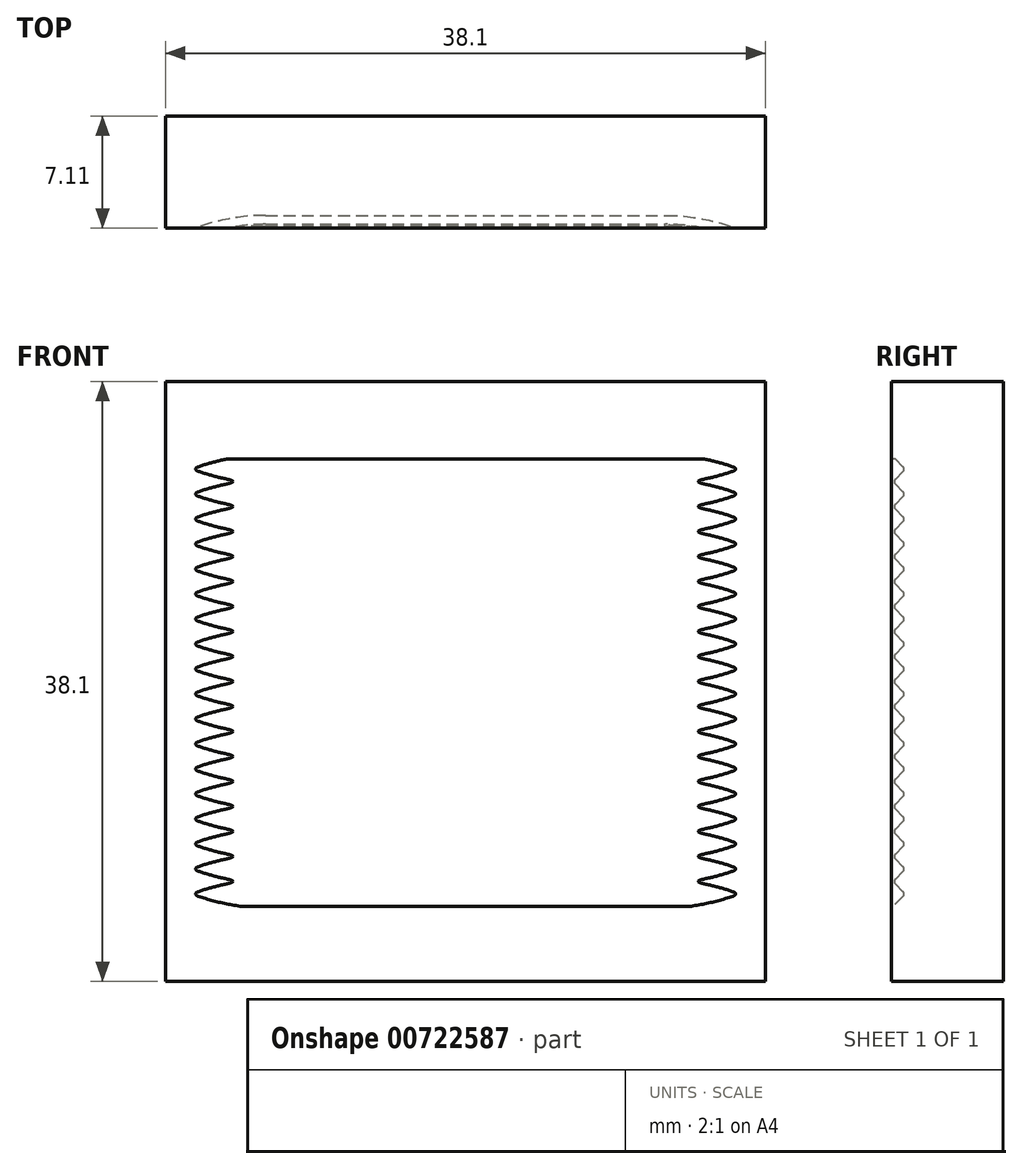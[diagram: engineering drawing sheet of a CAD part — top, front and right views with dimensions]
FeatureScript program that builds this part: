
annotation { "Feature Type Name" : "Feature", "Feature Type Description" : "" }
export const myFeature = defineFeature(function(context is Context, id is Id, definition is map)
    precondition{}
    {
        {
            var Q0;
            Q0=qCreatedBy(makeId("Front.planeOp"),FACE);
            var sketch = newSketch(context, id + "F0", { "sketchPlane" : qUnion([Q0])});
            skLineSegment(sketch, "E0", {"start": v(-12.7, -25.4) * mm, "end": v(-12.7, -12.7) * mm});
            skLineSegment(sketch, "E1", {"start": v(-12.7, 25.4) * mm, "end": v(12.7, 25.4) * mm});
            skLineSegment(sketch, "E2", {"start": v(12.7, 25.4) * mm, "end": v(12.7, 12.7) * mm});
            skLineSegment(sketch, "E3", {"start": v(12.7, -25.4) * mm, "end": v(-12.7, -25.4) * mm});
            skLineSegment(sketch, "E4", {"start": v(0, -25.4) * mm, "end": v(0, 25.4) * mm, "construction": true});
            skLineSegment(sketch, "E5", {"start": v(-12.7, 12.7) * mm, "end": v(12.7, 12.7) * mm, "construction": true});
            skLineSegment(sketch, "E6", {"start": v(-12.7, -12.7) * mm, "end": v(12.7, -12.7) * mm, "construction": true});
            skLineSegment(sketch, "E7", {"start": v(-25.4, 0) * mm, "end": v(25.4, 0) * mm, "construction": true});
            skPoint(sketch, "E8.orphan", {"position": v(0, 47.84) * mm});
            skLineSegment(sketch, "E9", {"start": v(-25.4, -12.7) * mm, "end": v(-25.4, 12.7) * mm});
            skLineSegment(sketch, "E10", {"start": v(-25.4, 12.7) * mm, "end": v(-12.7, 12.7) * mm});
            skLineSegment(sketch, "E11", {"start": v(25.4, 12.7) * mm, "end": v(25.4, -12.7) * mm});
            skLineSegment(sketch, "E12", {"start": v(25.4, -12.7) * mm, "end": v(12.7, -12.7) * mm});
            skLineSegment(sketch, "E13.trimOffspring", {"start": v(12.7, 12.7) * mm, "end": v(25.4, 12.7) * mm});
            skLineSegment(sketch, "E14.trimOffspring", {"start": v(12.7, -12.7) * mm, "end": v(12.7, -25.4) * mm});
            skLineSegment(sketch, "E15.trimOffspring", {"start": v(-12.7, 12.7) * mm, "end": v(-12.7, 25.4) * mm});
            skLineSegment(sketch, "E16.trimOffspring", {"start": v(-12.7, -12.7) * mm, "end": v(-25.4, -12.7) * mm});
            skLineSegment(sketch, "E17", {"start": v(-12.7, 12.7) * mm, "end": v(-12.7, -12.7) * mm, "construction": true});
            skLineSegment(sketch, "E18", {"start": v(12.7, 12.7) * mm, "end": v(12.7, -12.7) * mm, "construction": true});
            skCircle(sketch, "E19", {"center": v(0, 0) * mm, "radius": 12.7 * mm, "construction": true});
            skSolve(sketch);
        }
        {
            var Q0;
            Q0 = qSketchRegion(id + "F0", true);
            extrude(context, id + "F1", {"entities" : qUnion([Q0]), "depth" : 12.7 * mm, "offsetDistance" : 25.4 * mm});
        }
        {
            var Q0;
            Q0=qCreatedBy(makeId("Front.planeOp"),FACE);
            var sketch = newSketch(context, id + "F2", { "sketchPlane" : qUnion([Q0])});
            skLineSegment(sketch, "E20.bottom", {"start": v(-12.7, 12.7) * mm, "end": v(12.7, 12.7) * mm, "construction": true});
            skLineSegment(sketch, "E20.top", {"start": v(-12.7, -12.7) * mm, "end": v(12.7, -12.7) * mm, "construction": true});
            skLineSegment(sketch, "E20.left", {"start": v(-12.7, 12.7) * mm, "end": v(-12.7, -12.7) * mm, "construction": true});
            skLineSegment(sketch, "E20.right", {"start": v(12.7, 12.7) * mm, "end": v(12.7, -12.7) * mm, "construction": true});
            skLineSegment(sketch, "E21.bottom", {"start": v(19.05, 19.05) * mm, "end": v(-19.05, 19.05) * mm});
            skLineSegment(sketch, "E21.top", {"start": v(19.05, -19.05) * mm, "end": v(-19.05, -19.05) * mm});
            skLineSegment(sketch, "E21.left", {"start": v(19.05, 19.05) * mm, "end": v(19.05, -19.05) * mm});
            skLineSegment(sketch, "E21.right", {"start": v(-19.05, 19.05) * mm, "end": v(-19.05, -19.05) * mm});
            skLineSegment(sketch, "E22", {"start": v(-19.05, 19.05) * mm, "end": v(19.05, -19.05) * mm, "construction": true});
            skLineSegment(sketch, "E23", {"start": v(-19.05, -19.05) * mm, "end": v(19.05, 19.05) * mm, "construction": true});
            skSolve(sketch);
        }
        {
            var Q0;
            Q0=makeQuery(id+"F1.opExtrude","CAP_EDGE",EDGE,{"disambiguationData":[OSD([sQuery(id+"F0.wireOp",EDGE,"E9")])],"isStart":true});
            var Q1;
            Q1=makeQuery(id+"F1.opExtrude","CAP_EDGE",EDGE,{"disambiguationData":[OSD([sQuery(id+"F0.wireOp",EDGE,"E3")])],"isStart":true});
            var Q2;
            Q2=makeQuery(id+"F1.opExtrude","CAP_EDGE",EDGE,{"disambiguationData":[OSD([sQuery(id+"F0.wireOp",EDGE,"E1")])],"isStart":true});
            var Q3;
            Q3=makeQuery(id+"F1.opExtrude","CAP_EDGE",EDGE,{"disambiguationData":[OSD([sQuery(id+"F0.wireOp",EDGE,"E11")])],"isStart":true});
            fillet(context, id + "F3", {"entities" : qUnion([Q0, Q1, Q2, Q3]), "radius" : 12.7 * mm, "tangentPropagation" : true, "allowEdgeOverflow" : false});
        }
        {
            var Q0;
            Q0 = qSketchRegion(id + "F2", true);
            extrude(context, id + "F4", {"entities" : qUnion([Q0]), "oppositeDirection" : true, "depth" : 6.35 * mm, "offsetDistance" : 25.4 * mm, "hasSecondDirection" : true, "secondDirectionOppositeDirection" : false, "secondDirectionDepth" : 0.76 * mm});
        }
        {
            var Q0;
            Q0=makeQuery(id+"F1.opExtrude","CAP_FACE",FACE,{"disambiguationData":[OSD([sQuery(id+"F0.wireOp",EDGE,"E0"),sQuery(id+"F0.wireOp",EDGE,"E1"),sQuery(id+"F0.wireOp",EDGE,"E2"),sQuery(id+"F0.wireOp",EDGE,"E3"),sQuery(id+"F0.wireOp",EDGE,"E9"),sQuery(id+"F0.wireOp",EDGE,"E10"),sQuery(id+"F0.wireOp",EDGE,"E11"),sQuery(id+"F0.wireOp",EDGE,"E12"),sQuery(id+"F0.wireOp",EDGE,"E13.trimOffspring"),sQuery(id+"F0.wireOp",EDGE,"E14.trimOffspring"),sQuery(id+"F0.wireOp",EDGE,"E15.trimOffspring"),sQuery(id+"F0.wireOp",EDGE,"E16.trimOffspring")])],"isStart":false});
            var sketch = newSketch(context, id + "F5", { "sketchPlane" : qUnion([Q0])});
            skLineSegment(sketch, "E24", {"start": v(-24.88, -12.56) * mm, "end": v(-25.38, -12.05) * mm});
            skLineSegment(sketch, "E25", {"start": v(-24.88, -12.84) * mm, "end": v(-25.38, -13.35) * mm});
            skLineSegment(sketch, "E26", {"start": v(-19.18, -13.5) * mm, "end": v(-25.53, -13.5) * mm, "construction": true});
            skPoint(sketch, "E27.visualSharp", {"position": v(-24.73, -12.7) * mm});
            skArc(sketch, "E27.filletArc", {"start": v(-24.88, -12.84) * mm, "mid": v(-24.82, -12.7) * mm, "end": v(-24.88, -12.56) * mm});
            skLineSegment(sketch, "E28", {"start": v(-19.18, -14.29) * mm, "end": v(-19.18, 14.14) * mm});
            skLineSegment(sketch, "E29", {"start": v(-25.38, -13.64) * mm, "end": v(-24.73, -14.29) * mm});
            skLineSegment(sketch, "E30", {"start": v(-24.73, -14.29) * mm, "end": v(-19.18, -14.29) * mm});
            skPoint(sketch, "E31.visualSharp", {"position": v(-25.53, -13.5) * mm});
            skArc(sketch, "E31.filletArc", {"start": v(-25.38, -13.35) * mm, "mid": v(-25.44, -13.5) * mm, "end": v(-25.38, -13.64) * mm});
            skLineSegment(sketch, "E32", {"start": v(-19.18, 14.14) * mm, "end": v(-24.88, 14.14) * mm});
            skLineSegment(sketch, "E33", {"start": v(-25.53, -13.5) * mm, "end": v(-25.53, -11.9) * mm, "construction": true});
            skLineSegment(sketch, "E34", {"start": v(-25.38, -11.76) * mm, "end": v(-24.73, -11.11) * mm, "construction": true});
            skLineSegment(sketch, "E35", {"start": v(-24.73, -12.7) * mm, "end": v(-24.73, -11.11) * mm, "construction": true});
            skPoint(sketch, "E36.visualSharp", {"position": v(-25.53, -11.9) * mm});
            skArc(sketch, "E36.filletArc", {"start": v(-25.38, -11.76) * mm, "mid": v(-25.44, -11.9) * mm, "end": v(-25.38, -12.05) * mm});
            skLineSegment(sketch, "E37.0.1.0", {"start": v(-24.88, -11.26) * mm, "end": v(-25.38, -11.76) * mm});
            skArc(sketch, "E37.0.1.1", {"start": v(-24.88, -11.26) * mm, "mid": v(-24.82, -11.11) * mm, "end": v(-24.88, -10.97) * mm});
            skLineSegment(sketch, "E37.0.1.2", {"start": v(-24.88, -10.97) * mm, "end": v(-25.38, -10.46) * mm});
            skArc(sketch, "E37.0.1.3", {"start": v(-25.38, -10.18) * mm, "mid": v(-25.44, -10.32) * mm, "end": v(-25.38, -10.46) * mm});
            skLineSegment(sketch, "E37.0.2.0", {"start": v(-24.88, -9.67) * mm, "end": v(-25.38, -10.18) * mm});
            skArc(sketch, "E37.0.2.1", {"start": v(-24.88, -9.67) * mm, "mid": v(-24.82, -9.53) * mm, "end": v(-24.88, -9.38) * mm});
            skLineSegment(sketch, "E37.0.2.2", {"start": v(-24.88, -9.38) * mm, "end": v(-25.38, -8.87) * mm});
            skArc(sketch, "E37.0.2.3", {"start": v(-25.38, -8.59) * mm, "mid": v(-25.44, -8.73) * mm, "end": v(-25.38, -8.87) * mm});
            skLineSegment(sketch, "E37.0.3.0", {"start": v(-24.88, -8.08) * mm, "end": v(-25.38, -8.59) * mm});
            skArc(sketch, "E37.0.3.1", {"start": v(-24.88, -8.08) * mm, "mid": v(-24.82, -7.94) * mm, "end": v(-24.88, -7.8) * mm});
            skLineSegment(sketch, "E37.0.3.2", {"start": v(-24.88, -7.8) * mm, "end": v(-25.38, -7.29) * mm});
            skArc(sketch, "E37.0.3.3", {"start": v(-25.38, -7) * mm, "mid": v(-25.44, -7.14) * mm, "end": v(-25.38, -7.29) * mm});
            skLineSegment(sketch, "E37.0.4.0", {"start": v(-24.88, -6.5) * mm, "end": v(-25.38, -7) * mm});
            skArc(sketch, "E37.0.4.1", {"start": v(-24.88, -6.5) * mm, "mid": v(-24.82, -6.35) * mm, "end": v(-24.88, -6.2) * mm});
            skLineSegment(sketch, "E37.0.4.2", {"start": v(-24.88, -6.2) * mm, "end": v(-25.38, -5.7) * mm});
            skArc(sketch, "E37.0.4.3", {"start": v(-25.38, -5.41) * mm, "mid": v(-25.44, -5.56) * mm, "end": v(-25.38, -5.7) * mm});
            skLineSegment(sketch, "E37.0.5.0", {"start": v(-24.88, -4.9) * mm, "end": v(-25.38, -5.41) * mm});
            skArc(sketch, "E37.0.5.1", {"start": v(-24.88, -4.9) * mm, "mid": v(-24.82, -4.76) * mm, "end": v(-24.88, -4.62) * mm});
            skLineSegment(sketch, "E37.0.5.2", {"start": v(-24.88, -4.62) * mm, "end": v(-25.38, -4.11) * mm});
            skArc(sketch, "E37.0.5.3", {"start": v(-25.38, -3.83) * mm, "mid": v(-25.44, -3.97) * mm, "end": v(-25.38, -4.11) * mm});
            skLineSegment(sketch, "E37.0.6.0", {"start": v(-24.88, -3.32) * mm, "end": v(-25.38, -3.83) * mm});
            skArc(sketch, "E37.0.6.1", {"start": v(-24.88, -3.32) * mm, "mid": v(-24.82, -3.18) * mm, "end": v(-24.88, -3.03) * mm});
            skLineSegment(sketch, "E37.0.6.2", {"start": v(-24.88, -3.03) * mm, "end": v(-25.38, -2.52) * mm});
            skArc(sketch, "E37.0.6.3", {"start": v(-25.38, -2.24) * mm, "mid": v(-25.44, -2.38) * mm, "end": v(-25.38, -2.52) * mm});
            skLineSegment(sketch, "E37.0.7.0", {"start": v(-24.88, -1.73) * mm, "end": v(-25.38, -2.24) * mm});
            skArc(sketch, "E37.0.7.1", {"start": v(-24.88, -1.73) * mm, "mid": v(-24.82, -1.59) * mm, "end": v(-24.88, -1.44) * mm});
            skLineSegment(sketch, "E37.0.7.2", {"start": v(-24.88, -1.44) * mm, "end": v(-25.38, -0.94) * mm});
            skArc(sketch, "E37.0.7.3", {"start": v(-25.38, -0.65) * mm, "mid": v(-25.44, -0.8) * mm, "end": v(-25.38, -0.94) * mm});
            skLineSegment(sketch, "E37.0.8.0", {"start": v(-24.88, -0.14) * mm, "end": v(-25.38, -0.65) * mm});
            skArc(sketch, "E37.0.8.1", {"start": v(-24.88, -0.14) * mm, "mid": v(-24.82, 0) * mm, "end": v(-24.88, 0.14) * mm});
            skLineSegment(sketch, "E37.0.8.2", {"start": v(-24.88, 0.14) * mm, "end": v(-25.38, 0.65) * mm});
            skArc(sketch, "E37.0.8.3", {"start": v(-25.38, 0.94) * mm, "mid": v(-25.44, 0.8) * mm, "end": v(-25.38, 0.65) * mm});
            skLineSegment(sketch, "E37.0.9.0", {"start": v(-24.88, 1.44) * mm, "end": v(-25.38, 0.94) * mm});
            skArc(sketch, "E37.0.9.1", {"start": v(-24.88, 1.44) * mm, "mid": v(-24.82, 1.59) * mm, "end": v(-24.88, 1.73) * mm});
            skLineSegment(sketch, "E37.0.9.2", {"start": v(-24.88, 1.73) * mm, "end": v(-25.38, 2.24) * mm});
            skArc(sketch, "E37.0.9.3", {"start": v(-25.38, 2.52) * mm, "mid": v(-25.44, 2.38) * mm, "end": v(-25.38, 2.24) * mm});
            skLineSegment(sketch, "E37.0.10.0", {"start": v(-24.88, 3.03) * mm, "end": v(-25.38, 2.52) * mm});
            skArc(sketch, "E37.0.10.1", {"start": v(-24.88, 3.03) * mm, "mid": v(-24.82, 3.17) * mm, "end": v(-24.88, 3.32) * mm});
            skLineSegment(sketch, "E37.0.10.2", {"start": v(-24.88, 3.32) * mm, "end": v(-25.38, 3.83) * mm});
            skArc(sketch, "E37.0.10.3", {"start": v(-25.38, 4.11) * mm, "mid": v(-25.44, 3.97) * mm, "end": v(-25.38, 3.83) * mm});
            skLineSegment(sketch, "E37.0.11.0", {"start": v(-24.88, 4.62) * mm, "end": v(-25.38, 4.11) * mm});
            skArc(sketch, "E37.0.11.1", {"start": v(-24.88, 4.62) * mm, "mid": v(-24.82, 4.76) * mm, "end": v(-24.88, 4.9) * mm});
            skLineSegment(sketch, "E37.0.11.2", {"start": v(-24.88, 4.9) * mm, "end": v(-25.38, 5.41) * mm});
            skArc(sketch, "E37.0.11.3", {"start": v(-25.38, 5.7) * mm, "mid": v(-25.44, 5.56) * mm, "end": v(-25.38, 5.41) * mm});
            skLineSegment(sketch, "E37.0.12.0", {"start": v(-24.88, 6.2) * mm, "end": v(-25.38, 5.7) * mm});
            skArc(sketch, "E37.0.12.1", {"start": v(-24.88, 6.2) * mm, "mid": v(-24.82, 6.35) * mm, "end": v(-24.88, 6.5) * mm});
            skLineSegment(sketch, "E37.0.12.2", {"start": v(-24.88, 6.5) * mm, "end": v(-25.38, 7) * mm});
            skArc(sketch, "E37.0.12.3", {"start": v(-25.38, 7.29) * mm, "mid": v(-25.44, 7.14) * mm, "end": v(-25.38, 7) * mm});
            skLineSegment(sketch, "E37.0.13.0", {"start": v(-24.88, 7.8) * mm, "end": v(-25.38, 7.29) * mm});
            skArc(sketch, "E37.0.13.1", {"start": v(-24.88, 7.8) * mm, "mid": v(-24.82, 7.94) * mm, "end": v(-24.88, 8.08) * mm});
            skLineSegment(sketch, "E37.0.13.2", {"start": v(-24.88, 8.08) * mm, "end": v(-25.38, 8.59) * mm});
            skArc(sketch, "E37.0.13.3", {"start": v(-25.38, 8.87) * mm, "mid": v(-25.44, 8.73) * mm, "end": v(-25.38, 8.59) * mm});
            skLineSegment(sketch, "E37.0.14.0", {"start": v(-24.88, 9.38) * mm, "end": v(-25.38, 8.87) * mm});
            skArc(sketch, "E37.0.14.1", {"start": v(-24.88, 9.38) * mm, "mid": v(-24.82, 9.52) * mm, "end": v(-24.88, 9.67) * mm});
            skLineSegment(sketch, "E37.0.14.2", {"start": v(-24.88, 9.67) * mm, "end": v(-25.38, 10.18) * mm});
            skArc(sketch, "E37.0.14.3", {"start": v(-25.38, 10.46) * mm, "mid": v(-25.44, 10.32) * mm, "end": v(-25.38, 10.18) * mm});
            skLineSegment(sketch, "E37.0.15.0", {"start": v(-24.88, 10.97) * mm, "end": v(-25.38, 10.46) * mm});
            skArc(sketch, "E37.0.15.1", {"start": v(-24.88, 10.97) * mm, "mid": v(-24.82, 11.11) * mm, "end": v(-24.88, 11.26) * mm});
            skLineSegment(sketch, "E37.0.15.2", {"start": v(-24.88, 11.26) * mm, "end": v(-25.38, 11.76) * mm});
            skArc(sketch, "E37.0.15.3", {"start": v(-25.38, 12.05) * mm, "mid": v(-25.44, 11.9) * mm, "end": v(-25.38, 11.76) * mm});
            skLineSegment(sketch, "E37.0.16.0", {"start": v(-24.88, 12.56) * mm, "end": v(-25.38, 12.05) * mm});
            skArc(sketch, "E37.0.16.1", {"start": v(-24.88, 12.56) * mm, "mid": v(-24.82, 12.7) * mm, "end": v(-24.88, 12.84) * mm});
            skLineSegment(sketch, "E37.0.16.2", {"start": v(-24.88, 12.84) * mm, "end": v(-25.38, 13.35) * mm});
            skArc(sketch, "E37.0.16.3", {"start": v(-25.38, 13.64) * mm, "mid": v(-25.44, 13.5) * mm, "end": v(-25.38, 13.35) * mm});
            skLineSegment(sketch, "E37.0.17.0", {"start": v(-24.88, 14.14) * mm, "end": v(-25.38, 13.64) * mm});
            skLineSegment(sketch, "E37.direction1", {"start": v(-25.38, -13.35) * mm, "end": v(0.02, -13.35) * mm, "construction": true});
            skLineSegment(sketch, "E37.direction2", {"start": v(-25.38, -13.35) * mm, "end": v(-25.38, -11.76) * mm, "construction": true});
            skSolve(sketch);
        }
        {
            var Q0;
            Q0=makeQuery(id+"F1.opExtrude","SWEPT_FACE",FACE,{"disambiguationData":[OSD([sQuery(id+"F0.wireOp",EDGE,"E13.trimOffspring")])]});
            var sketch = newSketch(context, id + "F6", { "sketchPlane" : qUnion([Q0])});
            skArc(sketch, "E38.0", {"start": v(-12.7, 0) * mm, "mid": v(-21.68, -3.72) * mm, "end": v(-25.4, -12.7) * mm});
            skArc(sketch, "E38.2", {"start": v(25.4, -12.7) * mm, "mid": v(21.68, -3.72) * mm, "end": v(12.7, 0) * mm});
            skLineSegment(sketch, "E39", {"start": v(-12.7, 0) * mm, "end": v(12.7, 0) * mm});
            skSolve(sketch);
        }
        {
            var Q0;
            Q0 = qSketchRegion(id + "F5", true);
            var Q1;
            Q1=sQuery(id+"F6.wireOp",EDGE,"E38.0");
            var Q2;
            Q2=sQuery(id+"F6.wireOp",EDGE,"E39");
            var Q3;
            Q3=sQuery(id+"F6.wireOp",EDGE,"E38.2");
            sweep(context, id + "F7", {"operationType" : NewBodyOperationType.REMOVE, "profiles" : qUnion([Q0]), "path" : qUnion([Q1, Q2, Q3])});
        }
        {
            var Q0;
            Q0=makeQuery(id+"F1.opExtrude","SWEPT_BODY",BODY,{"disambiguationData":[OSD([sQuery(id+"F0.wireOp",EDGE,"E0"),sQuery(id+"F0.wireOp",EDGE,"E1"),sQuery(id+"F0.wireOp",EDGE,"E2"),sQuery(id+"F0.wireOp",EDGE,"E3"),sQuery(id+"F0.wireOp",EDGE,"E9"),sQuery(id+"F0.wireOp",EDGE,"E10"),sQuery(id+"F0.wireOp",EDGE,"E11"),sQuery(id+"F0.wireOp",EDGE,"E12"),sQuery(id+"F0.wireOp",EDGE,"E13.trimOffspring"),sQuery(id+"F0.wireOp",EDGE,"E14.trimOffspring"),sQuery(id+"F0.wireOp",EDGE,"E15.trimOffspring"),sQuery(id+"F0.wireOp",EDGE,"E16.trimOffspring")])]});
            deleteBodies(context, id + "F8", {"entities" : qUnion([Q0])});
        }
    });
